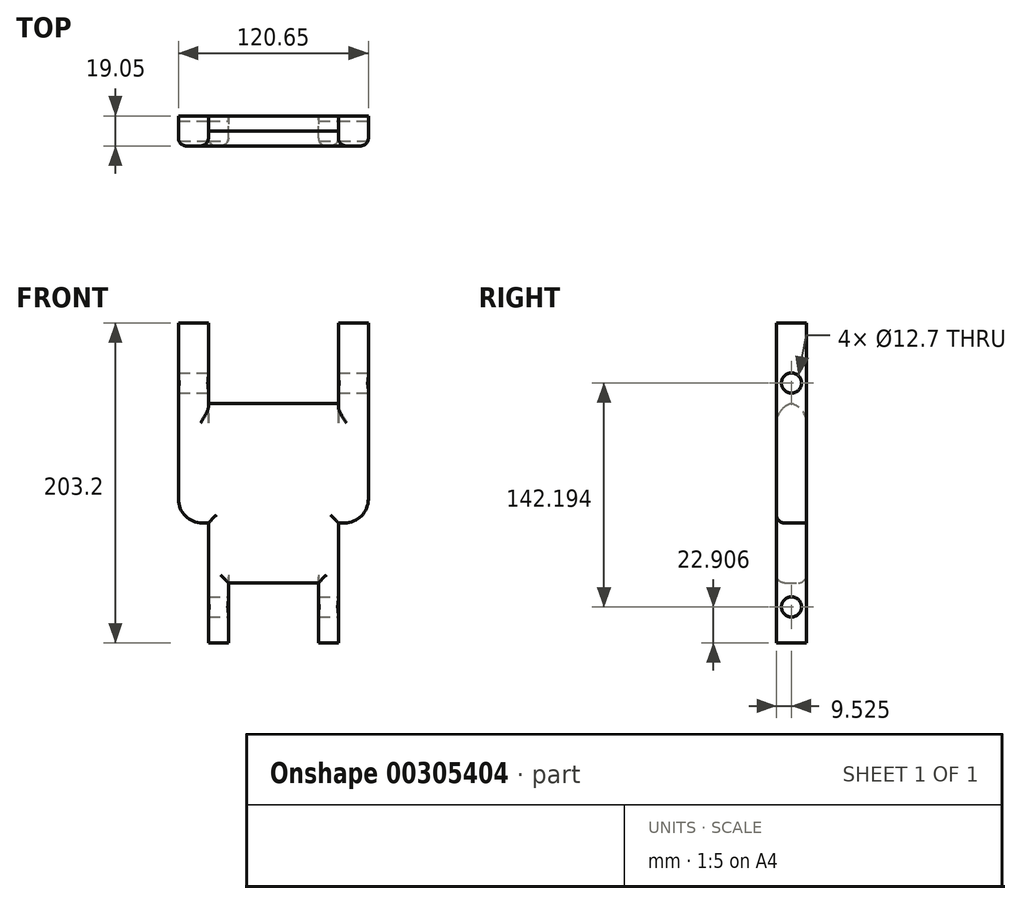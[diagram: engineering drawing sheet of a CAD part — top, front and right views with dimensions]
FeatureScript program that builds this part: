
annotation { "Feature Type Name" : "Feature", "Feature Type Description" : "" }
export const myFeature = defineFeature(function(context is Context, id is Id, definition is map)
    precondition{}
    {
        {
            var Q0;
            Q0=qCreatedBy(makeId("Front.planeOp"),FACE);
            var sketch = newSketch(context, id + "F0", { "sketchPlane" : qUnion([Q0])});
            skLineSegment(sketch, "E0.top", {"start": v(0, 38.1) * mm, "end": v(57.15, 38.1) * mm});
            skLineSegment(sketch, "E0.left", {"start": v(0, 0) * mm, "end": v(0, 38.1) * mm});
            skLineSegment(sketch, "E0.right", {"start": v(57.15, 0) * mm, "end": v(57.15, 38.1) * mm});
            skLineSegment(sketch, "E1.bottom", {"start": v(-12.7, 152.4) * mm, "end": v(69.85, 152.4) * mm});
            skLineSegment(sketch, "E1.top", {"start": v(-12.7, 0) * mm, "end": v(0, 0) * mm});
            skLineSegment(sketch, "E1.left", {"start": v(-12.7, 152.4) * mm, "end": v(-12.7, 0) * mm});
            skLineSegment(sketch, "E1.right", {"start": v(69.85, 152.4) * mm, "end": v(69.85, 0) * mm});
            skLineSegment(sketch, "E2", {"start": v(28.57, 152.4) * mm, "end": v(28.57, 38.1) * mm, "construction": true});
            skLineSegment(sketch, "E3.trimOffspring", {"start": v(57.15, 0) * mm, "end": v(69.85, 0) * mm});
            skPoint(sketch, "E4.orphan", {"position": v(28.57, 0) * mm});
            skSolve(sketch);
        }
        {
            var Q0;
            Q0 = qSketchRegion(id + "F0", true);
            extrude(context, id + "F1", {"entities" : qUnion([Q0]), "depth" : 19.05 * mm});
        }
        {
            var Q0;
            Q0=makeQuery(id+"F1.opExtrude","SWEPT_FACE",FACE,{"disambiguationData":[OSD([sQuery(id+"F0.wireOp",EDGE,"E0.left")])]});
            var sketch = newSketch(context, id + "F2", { "sketchPlane" : qUnion([Q0])});
            skPoint(sketch, "E5", {"position": v(0, 19.05) * mm});
            skLineSegment(sketch, "E6", {"start": v(0, 19.05) * mm, "end": v(-19.05, 19.05) * mm});
            skCircle(sketch, "E7", {"center": v(-9.53, 22.9) * mm, "radius": 6.35 * mm});
            skLineSegment(sketch, "E8", {"start": v(-9.53, 19.05) * mm, "end": v(-9.53, 38.1) * mm, "construction": true});
            skLineSegment(sketch, "E9", {"start": v(-19.05, 22.9) * mm, "end": v(0, 22.9) * mm, "construction": true});
            skSolve(sketch);
        }
        {
            var Q0;
            Q0=makeQuery(id+"F2.imprint","IMPRINT",FACE,{"disambiguationData":[TD([[makeQuery(id+"F2.imprint","IMPRINT",EDGE,{"derivedFrom":sQuery(id+"F2.wireOp",EDGE,"E7")}),1.0]])]});
            extrude(context, id + "F3", {"entities" : qUnion([Q0]), "operationType" : NewBodyOperationType.REMOVE, "oppositeDirection" : true, "depth" : 25.4 * mm, "hasSecondDirection" : true, "secondDirectionBound" : SecondDirectionBoundingType.THROUGH_ALL, "secondDirectionOppositeDirection" : false, "secondDirectionDepth" : 25.4 * mm});
        }
        {
            var Q0;
            Q0=makeQuery(id+"F1.opExtrude","CAP_EDGE",EDGE,{"disambiguationData":[OSD([sQuery(id+"F0.wireOp",EDGE,"E0.top")])],"isStart":false});
            var Q1;
            Q1=makeQuery(id+"F1.opExtrude","CAP_EDGE",EDGE,{"disambiguationData":[OSD([sQuery(id+"F0.wireOp",EDGE,"E0.top")])],"isStart":true});
            fillet(context, id + "F4", {"entities" : qUnion([Q0, Q1]), "radius" : 5.08 * mm, "tangentPropagation" : true, "allowEdgeOverflow" : false});
        }
        {
            var Q0;
            Q0=makeQuery(id+"F1.opExtrude","SWEPT_FACE",FACE,{"disambiguationData":[OSD([sQuery(id+"F0.wireOp",EDGE,"E1.right")])]});
            var sketch = newSketch(context, id + "F5", { "sketchPlane" : qUnion([Q0])});
            skLineSegment(sketch, "E10.bottom", {"start": v(-19.05, 76.2) * mm, "end": v(0, 76.2) * mm});
            skLineSegment(sketch, "E10.top", {"start": v(-19.05, 152.4) * mm, "end": v(0, 152.4) * mm});
            skLineSegment(sketch, "E10.left", {"start": v(-19.05, 76.2) * mm, "end": v(-19.05, 152.4) * mm});
            skLineSegment(sketch, "E10.right", {"start": v(0, 76.2) * mm, "end": v(0, 152.4) * mm});
            skLineSegment(sketch, "E11", {"start": v(-19.05, 76.2) * mm, "end": v(-19.05, 0) * mm});
            skSolve(sketch);
        }
        {
            var Q0;
            Q0=makeQuery(id+"F5.imprint","IMPRINT",FACE,{"disambiguationData":[TD([[makeQuery(id+"F5.imprint","IMPRINT",EDGE,{"derivedFrom":sQuery(id+"F5.wireOp",EDGE,"E10.bottom")}),1.0]])]});
            extrude(context, id + "F6", {"entities" : qUnion([Q0]), "operationType" : NewBodyOperationType.ADD, "depth" : 19.05 * mm});
        }
        {
            var Q0;
            Q0=makeQuery(id+"F1.opExtrude","SWEPT_FACE",FACE,{"disambiguationData":[OSD([sQuery(id+"F0.wireOp",EDGE,"E1.left")])]});
            var sketch = newSketch(context, id + "F7", { "sketchPlane" : qUnion([Q0])});
            skPoint(sketch, "E12.0", {"position": v(19.05, 114.3) * mm});
            skLineSegment(sketch, "E13.0", {"start": v(19.05, 152.4) * mm, "end": v(19.05, 76.2) * mm});
            skLineSegment(sketch, "E14.0.1", {"start": v(19.05, 76.2) * mm, "end": v(0, 76.2) * mm});
            skLineSegment(sketch, "E14.0.2", {"start": v(0, 76.2) * mm, "end": v(0, 152.4) * mm});
            skLineSegment(sketch, "E14.0.3", {"start": v(0, 152.4) * mm, "end": v(19.05, 152.4) * mm});
            skSolve(sketch);
        }
        {
            var Q0;
            Q0=makeQuery(id+"F7.imprint","IMPRINT",FACE,{"disambiguationData":[TD([[makeQuery(id+"F7.imprint","IMPRINT",EDGE,{"derivedFrom":sQuery(id+"F7.wireOp",EDGE,"E13.0")}),-1.0]])]});
            extrude(context, id + "F8", {"entities" : qUnion([Q0]), "operationType" : NewBodyOperationType.ADD, "depth" : 19.05 * mm});
        }
        {
            var Q0;
            Q0=makeQuery(id+"F8.boolean.opBoolean","MERGE",FACE,{"derivedFrom":[makeQuery(id+"F6.boolean.opBoolean","MERGE",FACE,{"derivedFrom":[makeQuery(id+"F1.opExtrude","SWEPT_FACE",FACE,{"disambiguationData":[OSD([sQuery(id+"F0.wireOp",EDGE,"E1.bottom")])]}),makeQuery(id+"F6.opExtrude","SWEPT_FACE",FACE,{"disambiguationData":[OSD([sQuery(id+"F5.wireOp",EDGE,"E10.top")])]})]}),makeQuery(id+"F8.opExtrude","SWEPT_FACE",FACE,{"disambiguationData":[OSD([sQuery(id+"F7.wireOp",EDGE,"E14.0.3")])]})]});
            var sketch = newSketch(context, id + "F9", { "sketchPlane" : qUnion([Q0])});
            skLineSegment(sketch, "E15.0", {"start": v(-31.75, 0) * mm, "end": v(-12.7, 0) * mm});
            skLineSegment(sketch, "E16.0", {"start": v(88.9, 0) * mm, "end": v(69.85, 0) * mm});
            skLineSegment(sketch, "E17.0", {"start": v(88.9, -19.05) * mm, "end": v(88.9, 0) * mm});
            skLineSegment(sketch, "E18.0", {"start": v(-31.75, -19.05) * mm, "end": v(-31.75, 0) * mm});
            skLineSegment(sketch, "E19", {"start": v(-12.7, 0) * mm, "end": v(-12.7, -19.05) * mm});
            skLineSegment(sketch, "E20", {"start": v(-12.7, -19.05) * mm, "end": v(-31.75, -19.05) * mm});
            skLineSegment(sketch, "E21", {"start": v(69.85, 0) * mm, "end": v(69.85, -19.05) * mm});
            skLineSegment(sketch, "E22", {"start": v(69.85, -19.05) * mm, "end": v(88.9, -19.05) * mm});
            skSolve(sketch);
        }
        {
            var Q0;
            Q0=makeQuery(id+"F9.imprint","IMPRINT",FACE,{"disambiguationData":[TD([[makeQuery(id+"F9.imprint","IMPRINT",EDGE,{"derivedFrom":sQuery(id+"F9.wireOp",EDGE,"E18.0")}),-1.0]])]});
            var Q1;
            Q1=makeQuery(id+"F9.imprint","IMPRINT",FACE,{"disambiguationData":[TD([[makeQuery(id+"F9.imprint","IMPRINT",EDGE,{"derivedFrom":sQuery(id+"F9.wireOp",EDGE,"E16.0")}),-1.0]])]});
            extrude(context, id + "F10", {"entities" : qUnion([Q0, Q1]), "operationType" : NewBodyOperationType.ADD, "depth" : 50.8 * mm});
        }
        {
            var Q0;
            Q0=makeQuery(id+"F10.opExtrude","SWEPT_FACE",FACE,{"disambiguationData":[OSD([sQuery(id+"F9.wireOp",EDGE,"E19")])]});
            var sketch = newSketch(context, id + "F11", { "sketchPlane" : qUnion([Q0])});
            skCircle(sketch, "E23", {"center": v(-9.53, 165.1) * mm, "radius": 6.35 * mm});
            skPoint(sketch, "E24.start.orphan", {"position": v(0, 165.1) * mm});
            skPoint(sketch, "E25.start.orphan", {"position": v(-9.53, 177.8) * mm});
            skPoint(sketch, "E26.trimOffspring.end.orphan", {"position": v(-9.53, 152.4) * mm});
            skPoint(sketch, "E27.orphan", {"position": v(0, 177.8) * mm});
            skPoint(sketch, "E28.end.orphan", {"position": v(-19.05, 177.8) * mm});
            skSolve(sketch);
        }
        {
            var Q0;
            Q0=makeQuery(id+"F11.imprint","IMPRINT",FACE,{"disambiguationData":[TD([[makeQuery(id+"F11.imprint","IMPRINT",EDGE,{"derivedFrom":sQuery(id+"F11.wireOp",EDGE,"E23")}),1.0]])]});
            extrude(context, id + "F12", {"entities" : qUnion([Q0]), "operationType" : NewBodyOperationType.REMOVE, "endBound" : BoundingType.THROUGH_ALL, "oppositeDirection" : true, "depth" : 25.4 * mm, "hasSecondDirection" : true, "secondDirectionBound" : SecondDirectionBoundingType.THROUGH_ALL, "secondDirectionOppositeDirection" : false, "secondDirectionDepth" : 25.4 * mm});
        }
        {
            var Q0;
            Q0=makeQuery(id+"F8.boolean.opBoolean","MERGE",EDGE,{"derivedFrom":[makeQuery(id+"F6.boolean.opBoolean","MERGE",EDGE,{"derivedFrom":[makeQuery(id+"F1.opExtrude","CAP_EDGE",EDGE,{"disambiguationData":[OSD([sQuery(id+"F0.wireOp",EDGE,"E1.bottom")])],"isStart":true}),makeQuery(id+"F6.opExtrude","SWEPT_EDGE",EDGE,{"disambiguationData":[OSD([sQuery(id+"F5.wireOp",EDGE,"E10.top"),sQuery(id+"F5.wireOp",EDGE,"E10.right")])]})]}),makeQuery(id+"F8.opExtrude","SWEPT_EDGE",EDGE,{"disambiguationData":[OSD([sQuery(id+"F7.wireOp",EDGE,"E14.0.2"),sQuery(id+"F7.wireOp",EDGE,"E14.0.3")])]})]});
            var Q1;
            Q1=makeQuery(id+"F8.boolean.opBoolean","MERGE",EDGE,{"derivedFrom":[makeQuery(id+"F6.boolean.opBoolean","MERGE",EDGE,{"derivedFrom":[makeQuery(id+"F1.opExtrude","CAP_EDGE",EDGE,{"disambiguationData":[OSD([sQuery(id+"F0.wireOp",EDGE,"E1.bottom")])],"isStart":false}),makeQuery(id+"F6.opExtrude","SWEPT_EDGE",EDGE,{"disambiguationData":[OSD([sQuery(id+"F5.wireOp",EDGE,"E10.top"),sQuery(id+"F5.wireOp",EDGE,"E10.left")])]})]}),makeQuery(id+"F8.opExtrude","SWEPT_EDGE",EDGE,{"disambiguationData":[OSD([sQuery(id+"F7.wireOp",EDGE,"E13.0"),sQuery(id+"F7.wireOp",EDGE,"E14.0.3")])]})]});
            fillet(context, id + "F13", {"entities" : qUnion([Q0, Q1]), "radius" : 12.7 * mm, "tangentPropagation" : true, "allowEdgeOverflow" : false});
        }
        {
            var Q0;
            Q0=makeQuery(id+"F6.opExtrude","CAP_EDGE",EDGE,{"disambiguationData":[OSD([sQuery(id+"F5.wireOp",EDGE,"E10.bottom")])],"isStart":false});
            var Q1;
            Q1=makeQuery(id+"F8.opExtrude","CAP_EDGE",EDGE,{"disambiguationData":[OSD([sQuery(id+"F7.wireOp",EDGE,"E14.0.1")])],"isStart":false});
            fillet(context, id + "F14", {"entities" : qUnion([Q0, Q1]), "radius" : 15.24 * mm, "tangentPropagation" : true, "allowEdgeOverflow" : false});
        }
        {
            var Q0;
            Q0=makeQuery(id+"F10.boolean.opBoolean","MERGE",EDGE,{"derivedFrom":[makeQuery(id+"F8.opExtrude","CAP_EDGE",EDGE,{"disambiguationData":[OSD([sQuery(id+"F7.wireOp",EDGE,"E13.0")])],"isStart":false}),makeQuery(id+"F10.opExtrude","SWEPT_EDGE",EDGE,{"disambiguationData":[OSD([sQuery(id+"F9.wireOp",EDGE,"E18.0"),sQuery(id+"F9.wireOp",EDGE,"E20")])]})]});
            var Q1;
            Q1=makeQuery(id+"F10.boolean.opBoolean","MERGE",EDGE,{"derivedFrom":[makeQuery(id+"F6.opExtrude","CAP_EDGE",EDGE,{"disambiguationData":[OSD([sQuery(id+"F5.wireOp",EDGE,"E10.left")])],"isStart":false}),makeQuery(id+"F10.opExtrude","SWEPT_EDGE",EDGE,{"disambiguationData":[OSD([sQuery(id+"F9.wireOp",EDGE,"E17.0"),sQuery(id+"F9.wireOp",EDGE,"E22")])]})]});
            var Q2;
            Q2=makeQuery(id+"F10.opExtrude","SWEPT_EDGE",EDGE,{"disambiguationData":[OSD([sQuery(id+"F0.wireOp",EDGE,"E1.bottom"),sQuery(id+"F5.wireOp",EDGE,"E10.top"),sQuery(id+"F5.wireOp",EDGE,"E10.left"),sQuery(id+"F7.wireOp",EDGE,"E13.0"),sQuery(id+"F7.wireOp",EDGE,"E14.0.3"),sQuery(id+"F9.wireOp",EDGE,"E21"),sQuery(id+"F9.wireOp",EDGE,"E22")])]});
            var Q3;
            Q3=makeQuery(id+"F10.opExtrude","SWEPT_EDGE",EDGE,{"disambiguationData":[OSD([sQuery(id+"F0.wireOp",EDGE,"E1.bottom"),sQuery(id+"F5.wireOp",EDGE,"E10.top"),sQuery(id+"F5.wireOp",EDGE,"E10.left"),sQuery(id+"F7.wireOp",EDGE,"E13.0"),sQuery(id+"F7.wireOp",EDGE,"E14.0.3"),sQuery(id+"F9.wireOp",EDGE,"E19"),sQuery(id+"F9.wireOp",EDGE,"E20")])]});
            var Q4;
            Q4=makeQuery(id+"F1.opExtrude","CAP_EDGE",EDGE,{"disambiguationData":[OSD([sQuery(id+"F0.wireOp",EDGE,"E1.left")])],"isStart":false});
            var Q5;
            Q5=makeQuery(id+"F1.opExtrude","CAP_EDGE",EDGE,{"disambiguationData":[OSD([sQuery(id+"F0.wireOp",EDGE,"E1.right")])],"isStart":false});
            var Q6;
            Q6=makeQuery(id+"F1.opExtrude","CAP_EDGE",EDGE,{"disambiguationData":[OSD([sQuery(id+"F0.wireOp",EDGE,"E0.right")])],"isStart":false});
            var Q7;
            Q7=makeQuery(id+"F1.opExtrude","CAP_EDGE",EDGE,{"disambiguationData":[OSD([sQuery(id+"F0.wireOp",EDGE,"E0.left")])],"isStart":false});
            fillet(context, id + "F15", {"entities" : qUnion([Q0, Q1, Q2, Q3, Q4, Q5, Q6, Q7]), "radius" : 5.08 * mm, "tangentPropagation" : true, "allowEdgeOverflow" : false});
        }
    });
